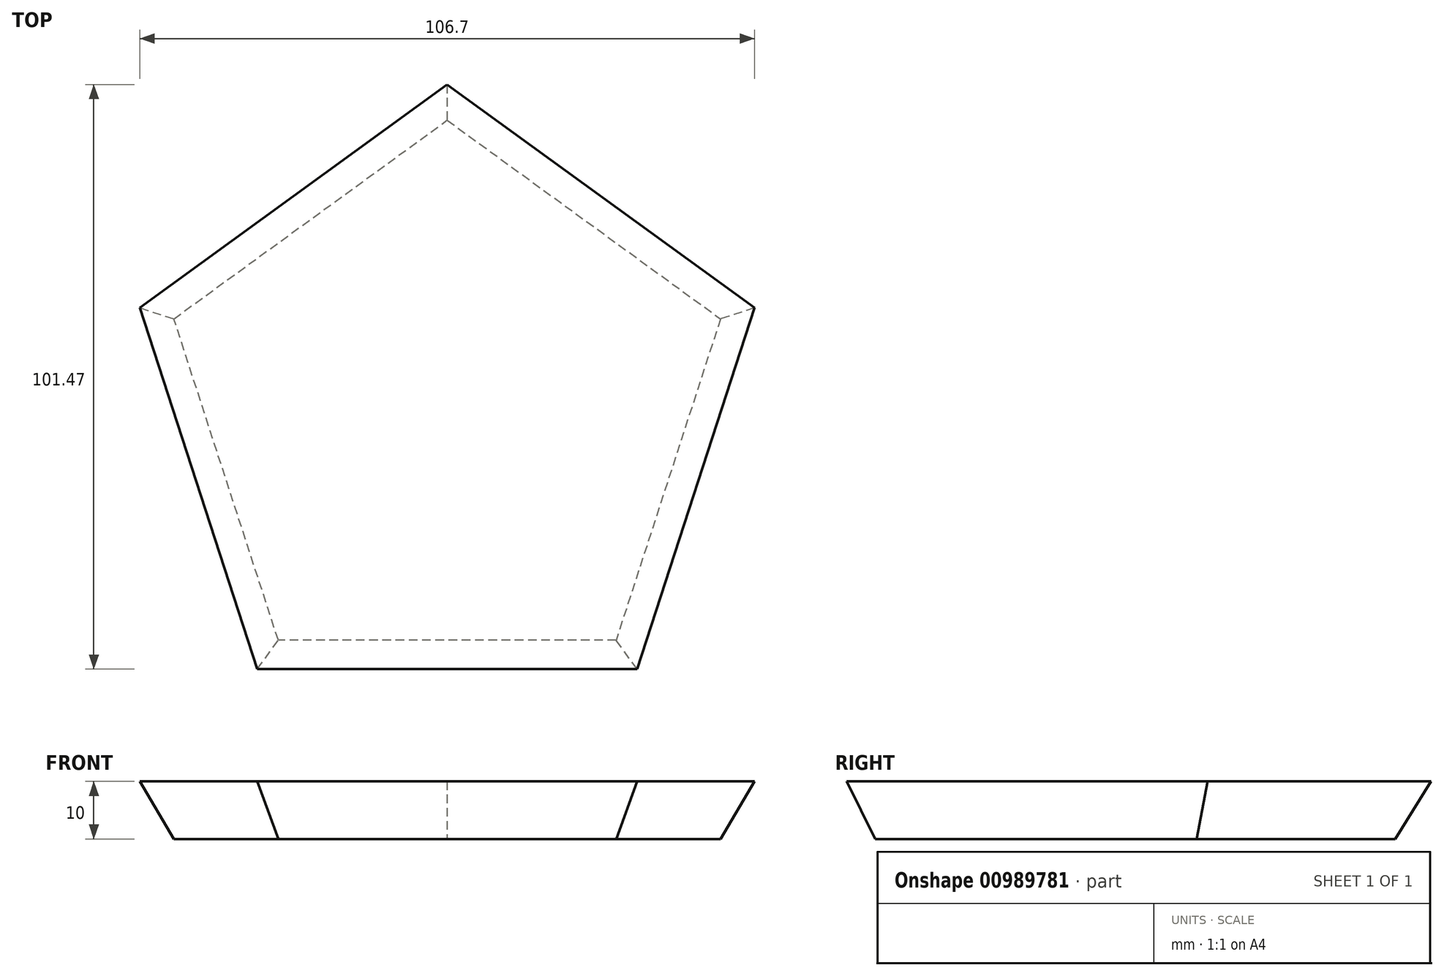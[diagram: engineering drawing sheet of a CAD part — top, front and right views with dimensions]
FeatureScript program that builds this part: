
annotation { "Feature Type Name" : "Feature", "Feature Type Description" : "" }
export const myFeature = defineFeature(function(context is Context, id is Id, definition is map)
    precondition{}
    {
        {
            var Q0;
            Q0=qCreatedBy(makeId("Top.planeOp"),FACE);
            var sketch = newSketch(context, id + "F0", { "sketchPlane" : qUnion([Q0])});
            skCircle(sketch, "E0.cCircle", {"center": v(0, 0) * mm, "radius": 40.38 * mm, "construction": true});
            skLineSegment(sketch, "E0.0", {"start": v(-47.47, 15.42) * mm, "end": v(0, 49.91) * mm});
            skLineSegment(sketch, "E0.1", {"start": v(0, 49.91) * mm, "end": v(47.47, 15.42) * mm});
            skLineSegment(sketch, "E0.2", {"start": v(47.47, 15.42) * mm, "end": v(29.34, -40.38) * mm});
            skLineSegment(sketch, "E0.3", {"start": v(29.34, -40.38) * mm, "end": v(-29.34, -40.38) * mm});
            skLineSegment(sketch, "E0.4", {"start": v(-29.34, -40.38) * mm, "end": v(-47.47, 15.42) * mm});
            skPoint(sketch, "E0.0.midPoint", {"position": v(-23.73, 32.67) * mm});
            skSolve(sketch);
        }
        {
            var Q0;
            Q0 = qSketchRegion(id + "F0", true);
            extrude(context, id + "F1", {"entities" : qUnion([Q0]), "depth" : 10 * mm, "offsetDistance" : 25.4 * mm, "hasDraft" : true, "draftAngle" : 26.57 * degree});
        }
    });
